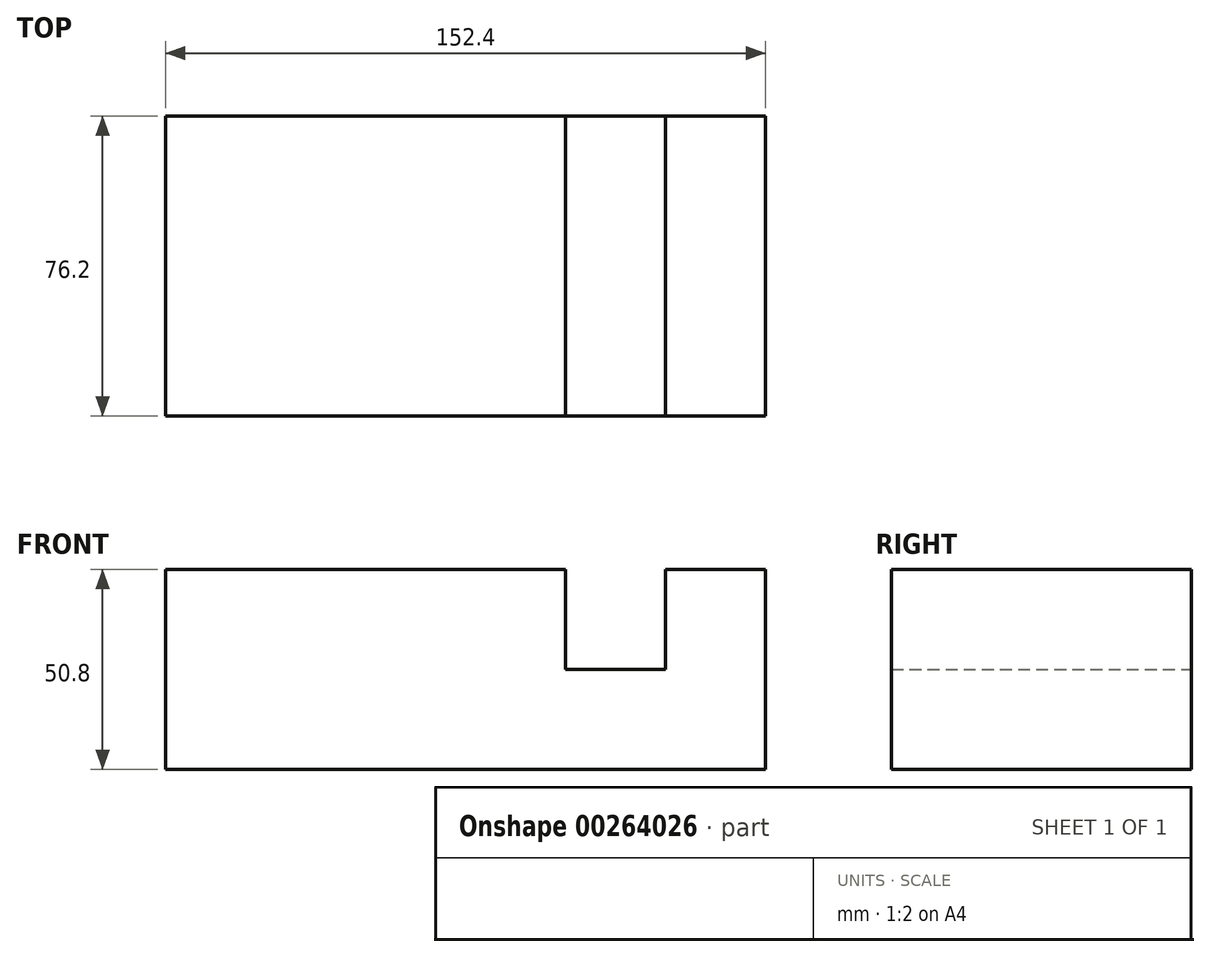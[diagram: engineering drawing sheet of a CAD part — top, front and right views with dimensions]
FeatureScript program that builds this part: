
annotation { "Feature Type Name" : "Feature", "Feature Type Description" : "" }
export const myFeature = defineFeature(function(context is Context, id is Id, definition is map)
    precondition{}
    {
        {
            var Q0;
            Q0=qCreatedBy(makeId("Front.planeOp"),FACE);
            var sketch = newSketch(context, id + "F0", { "sketchPlane" : qUnion([Q0])});
            skLineSegment(sketch, "E0", {"start": v(-76.27, 0) * mm, "end": v(76.13, 0) * mm});
            skLineSegment(sketch, "E1", {"start": v(76.13, 0) * mm, "end": v(76.13, 50.8) * mm});
            skLineSegment(sketch, "E2", {"start": v(50.73, 50.8) * mm, "end": v(76.13, 50.8) * mm});
            skLineSegment(sketch, "E3", {"start": v(50.73, 50.8) * mm, "end": v(50.73, 25.4) * mm});
            skLineSegment(sketch, "E4", {"start": v(25.33, 25.4) * mm, "end": v(50.73, 25.4) * mm});
            skLineSegment(sketch, "E5", {"start": v(25.33, 25.4) * mm, "end": v(25.33, 50.8) * mm});
            skLineSegment(sketch, "E6", {"start": v(-76.27, 50.8) * mm, "end": v(25.33, 50.8) * mm});
            skLineSegment(sketch, "E7", {"start": v(-76.27, 50.8) * mm, "end": v(-76.27, 0) * mm});
            skSolve(sketch);
        }
        {
            var Q0;
            Q0=makeQuery(id+"F0.imprint","IMPRINT",FACE,{"disambiguationData":[TD([[makeQuery(id+"F0.imprint","IMPRINT",EDGE,{"derivedFrom":sQuery(id+"F0.wireOp",EDGE,"E0")}),1.0]])]});
            extrude(context, id + "F1", {"entities" : qUnion([Q0]), "depth" : 76.2 * mm});
        }
    });
